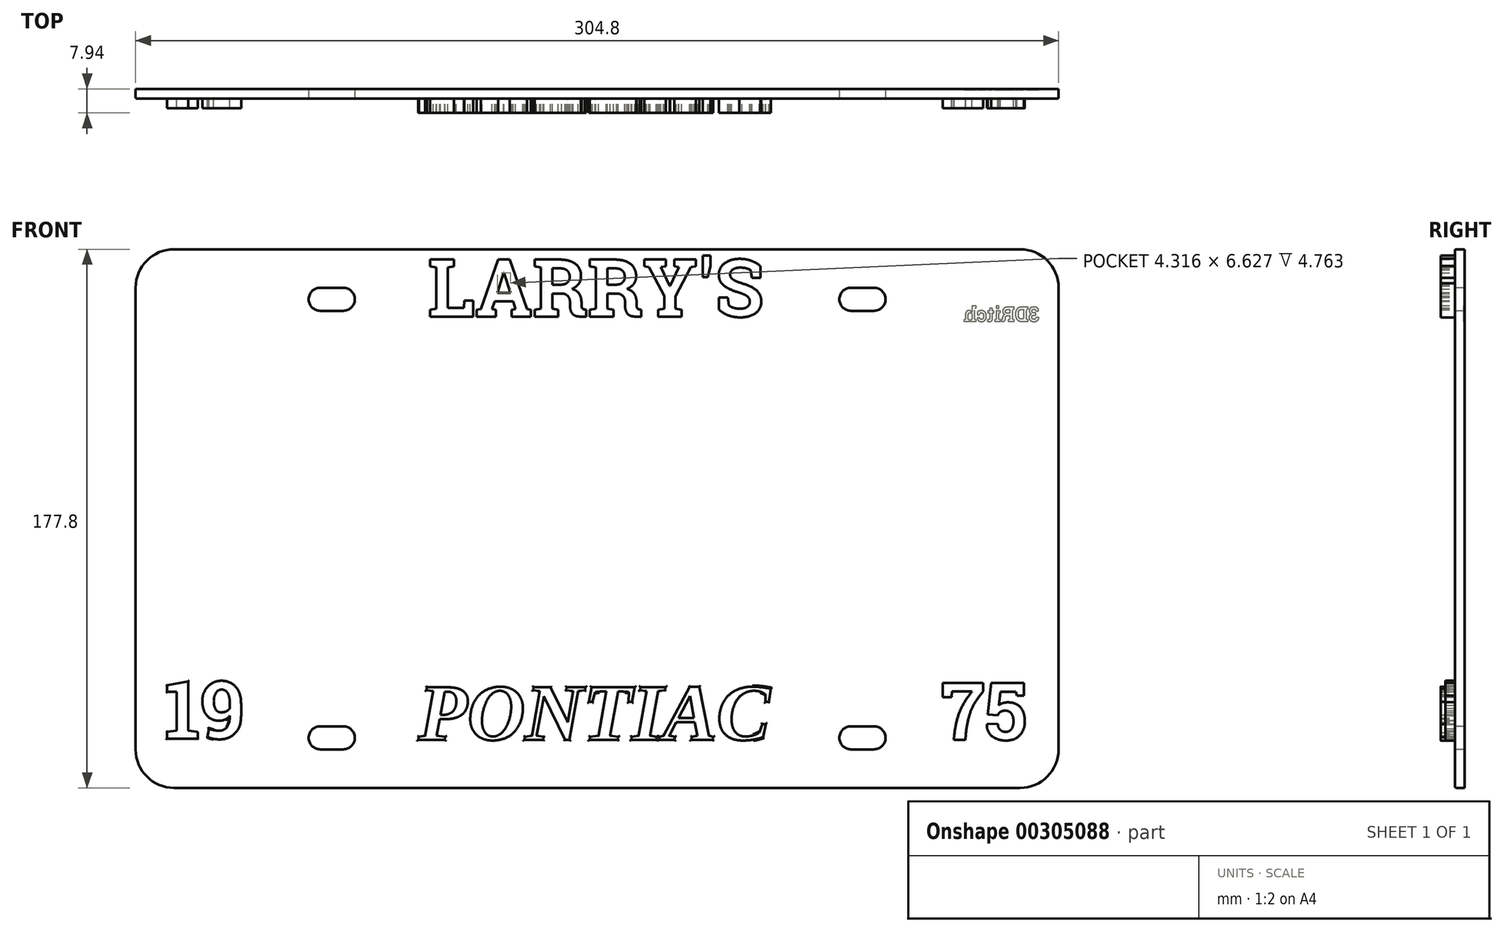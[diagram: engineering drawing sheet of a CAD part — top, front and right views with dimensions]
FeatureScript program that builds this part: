
annotation { "Feature Type Name" : "Feature", "Feature Type Description" : "" }
export const myFeature = defineFeature(function(context is Context, id is Id, definition is map)
    precondition{}
    {
        {
            var Q0;
            Q0=qCreatedBy(makeId("Front.planeOp"),FACE);
            var sketch = newSketch(context, id + "F0", { "sketchPlane" : qUnion([Q0])});
            skLineSegment(sketch, "E0.bottom", {"start": v(139.7, -88.9) * mm, "end": v(-139.7, -88.9) * mm});
            skLineSegment(sketch, "E0.top", {"start": v(139.7, 88.9) * mm, "end": v(-139.7, 88.9) * mm});
            skLineSegment(sketch, "E0.left", {"start": v(152.4, -76.2) * mm, "end": v(152.4, 76.2) * mm});
            skLineSegment(sketch, "E0.right", {"start": v(-152.4, -76.2) * mm, "end": v(-152.4, 76.2) * mm});
            skPoint(sketch, "E0.middle", {"position": v(0, 0) * mm});
            skLineSegment(sketch, "E1.bottom", {"start": v(-91.44, 76.2) * mm, "end": v(-83.82, 76.2) * mm, "construction": true});
            skLineSegment(sketch, "E1.top", {"start": v(-91.44, 68.58) * mm, "end": v(-83.82, 68.58) * mm, "construction": true});
            skPoint(sketch, "E1.middle", {"position": v(-87.63, 72.4) * mm});
            skPoint(sketch, "E2.visualSharp", {"position": v(-152.4, 88.9) * mm});
            skArc(sketch, "E2.filletArc", {"start": v(-139.7, 88.9) * mm, "mid": v(-148.68, 85.18) * mm, "end": v(-152.4, 76.2) * mm});
            skPoint(sketch, "E3.visualSharp", {"position": v(152.4, 88.9) * mm});
            skArc(sketch, "E3.filletArc", {"start": v(152.4, 76.2) * mm, "mid": v(148.68, 85.18) * mm, "end": v(139.7, 88.9) * mm});
            skPoint(sketch, "E4.visualSharp", {"position": v(152.4, -88.9) * mm});
            skArc(sketch, "E4.filletArc", {"start": v(139.7, -88.9) * mm, "mid": v(148.68, -85.18) * mm, "end": v(152.4, -76.2) * mm});
            skPoint(sketch, "E5.visualSharp", {"position": v(-152.4, -88.9) * mm});
            skArc(sketch, "E5.filletArc", {"start": v(-152.4, -76.2) * mm, "mid": v(-148.68, -85.18) * mm, "end": v(-139.7, -88.9) * mm});
            skArc(sketch, "E6", {"start": v(-91.44, 76.2) * mm, "mid": v(-95.25, 72.4) * mm, "end": v(-91.44, 68.58) * mm, "construction": true});
            skArc(sketch, "E7", {"start": v(-83.82, 68.58) * mm, "mid": v(-80.01, 72.39) * mm, "end": v(-83.82, 76.2) * mm, "construction": true});
            skSolve(sketch);
        }
        {
            var Q0;
            Q0=makeQuery(id+"F0.imprint","IMPRINT",FACE,{"disambiguationData":[TD([[makeQuery(id+"F0.imprint","IMPRINT",EDGE,{"derivedFrom":sQuery(id+"F0.wireOp",EDGE,"E0.bottom")}),-1.0]])]});
            extrude(context, id + "F1", {"entities" : qUnion([Q0]), "depth" : 3.17 * mm});
        }
        {
            var Q0;
            Q0=makeQuery(id+"F1.opExtrude","CAP_FACE",FACE,{"disambiguationData":[OSD([sQuery(id+"F0.wireOp",EDGE,"E0.bottom"),sQuery(id+"F0.wireOp",EDGE,"E0.top"),sQuery(id+"F0.wireOp",EDGE,"E0.left"),sQuery(id+"F0.wireOp",EDGE,"E0.right"),sQuery(id+"F0.wireOp",EDGE,"E2.filletArc"),sQuery(id+"F0.wireOp",EDGE,"E3.filletArc"),sQuery(id+"F0.wireOp",EDGE,"E4.filletArc"),sQuery(id+"F0.wireOp",EDGE,"E5.filletArc")])],"isStart":false});
            var sketch = newSketch(context, id + "F2", { "sketchPlane" : qUnion([Q0])});
            skArc(sketch, "E8.0", {"start": v(-91.44, 76.2) * mm, "mid": v(-95.25, 72.4) * mm, "end": v(-91.44, 68.58) * mm});
            skArc(sketch, "E8.1", {"start": v(-83.82, 68.58) * mm, "mid": v(-80.01, 72.39) * mm, "end": v(-83.82, 76.2) * mm});
            skLineSegment(sketch, "E9.0", {"start": v(-91.44, 76.2) * mm, "end": v(-83.82, 76.2) * mm});
            skLineSegment(sketch, "E10.0", {"start": v(-91.44, 68.58) * mm, "end": v(-83.82, 68.58) * mm});
            skLineSegment(sketch, "E11.0.1.0", {"start": v(-91.44, -68.58) * mm, "end": v(-83.82, -68.58) * mm});
            skLineSegment(sketch, "E11.0.1.1", {"start": v(-91.44, -76.2) * mm, "end": v(-83.82, -76.2) * mm});
            skArc(sketch, "E11.0.1.2", {"start": v(-91.44, -68.58) * mm, "mid": v(-95.25, -72.39) * mm, "end": v(-91.44, -76.2) * mm});
            skArc(sketch, "E11.0.1.3", {"start": v(-83.82, -76.2) * mm, "mid": v(-80.01, -72.4) * mm, "end": v(-83.82, -68.58) * mm});
            skLineSegment(sketch, "E11.1.0.0", {"start": v(83.82, 76.2) * mm, "end": v(91.44, 76.2) * mm});
            skLineSegment(sketch, "E11.1.0.1", {"start": v(83.82, 68.58) * mm, "end": v(91.44, 68.58) * mm});
            skArc(sketch, "E11.1.0.2", {"start": v(83.82, 76.2) * mm, "mid": v(80.01, 72.4) * mm, "end": v(83.82, 68.58) * mm});
            skArc(sketch, "E11.1.0.3", {"start": v(91.44, 68.58) * mm, "mid": v(95.25, 72.39) * mm, "end": v(91.44, 76.2) * mm});
            skLineSegment(sketch, "E11.1.1.0", {"start": v(83.82, -68.58) * mm, "end": v(91.44, -68.58) * mm});
            skLineSegment(sketch, "E11.1.1.1", {"start": v(83.82, -76.2) * mm, "end": v(91.44, -76.2) * mm});
            skArc(sketch, "E11.1.1.2", {"start": v(83.82, -68.58) * mm, "mid": v(80.01, -72.39) * mm, "end": v(83.82, -76.2) * mm});
            skArc(sketch, "E11.1.1.3", {"start": v(91.44, -76.2) * mm, "mid": v(95.25, -72.4) * mm, "end": v(91.44, -68.58) * mm});
            skLineSegment(sketch, "E11.direction1", {"start": v(-91.44, 76.2) * mm, "end": v(83.82, 76.2) * mm, "construction": true});
            skLineSegment(sketch, "E11.direction2", {"start": v(-91.44, 76.2) * mm, "end": v(-91.44, -68.58) * mm, "construction": true});
            skSolve(sketch);
        }
        {
            var Q0;
            Q0=makeQuery(id+"F2.imprint","IMPRINT",FACE,{"disambiguationData":[TD([[makeQuery(id+"F2.imprint","IMPRINT",EDGE,{"derivedFrom":sQuery(id+"F2.wireOp",EDGE,"E8.0")}),1.0]])]});
            var Q1;
            Q1=makeQuery(id+"F2.imprint","IMPRINT",FACE,{"disambiguationData":[TD([[makeQuery(id+"F2.imprint","IMPRINT",EDGE,{"derivedFrom":sQuery(id+"F2.wireOp",EDGE,"E11.0.1.0")}),-1.0]])]});
            var Q2;
            Q2=makeQuery(id+"F2.imprint","IMPRINT",FACE,{"disambiguationData":[TD([[makeQuery(id+"F2.imprint","IMPRINT",EDGE,{"derivedFrom":sQuery(id+"F2.wireOp",EDGE,"E11.1.1.0")}),-1.0]])]});
            var Q3;
            Q3=makeQuery(id+"F2.imprint","IMPRINT",FACE,{"disambiguationData":[TD([[makeQuery(id+"F2.imprint","IMPRINT",EDGE,{"derivedFrom":sQuery(id+"F2.wireOp",EDGE,"E11.1.0.0")}),-1.0]])]});
            var Q4;
            Q4=sQuery(id+"F2.wireOp",EDGE,"E9.0");
            extrude(context, id + "F3", {"entities" : qUnion([Q0, Q1, Q2, Q3]), "operationType" : NewBodyOperationType.REMOVE, "surfaceEntities" : qUnion([Q4]), "endBound" : BoundingType.THROUGH_ALL, "oppositeDirection" : true, "depth" : 25.4 * mm});
        }
        {
            var Q0;
            {var subQ0=sQuery(id+"F0.wireOp",EDGE,"E5.filletArc");var subQ1=sQuery(id+"F0.wireOp",EDGE,"E4.filletArc");var subQ2=sQuery(id+"F0.wireOp",EDGE,"E0.left");var subQ3=sQuery(id+"F0.wireOp",EDGE,"E0.top");var subQ4=sQuery(id+"F0.wireOp",EDGE,"E0.right");var subQ5=sQuery(id+"F0.wireOp",EDGE,"E2.filletArc");var subQ6=sQuery(id+"F0.wireOp",EDGE,"E0.bottom");var subQ7=sQuery(id+"F0.wireOp",EDGE,"E3.filletArc");Q0=makeQuery(id+"FR5AeGaN4UOH5Dw_1.boolean.opBoolean","SPLIT",FACE,{"disambiguationData":[TD([makeQuery(id+"F1.opExtrude","SWEPT_FACE",FACE,{"disambiguationData":[OSD([subQ6])]})])],"derivedFrom":makeQuery(id+"F1.opExtrude","CAP_FACE",FACE,{"disambiguationData":[OSD([subQ6,subQ3,subQ2,subQ4,subQ5,subQ7,subQ1,subQ0])],"isStart":false})});}
            var sketch = newSketch(context, id + "F4", { "sketchPlane" : qUnion([Q0])});
            skText(sketch, "E12", { "text": "PONTIAC", "fontName": "Tinos-BoldItalic.ttf"});
            const initialGuessF4  = {"E12": [-0.05902, -0.07303, 1, 0, 0.01905]};
            skSetInitialGuess(sketch, initialGuessF4);
            skSolve(sketch);
        }
        {
            var Q0;
            Q0=qSketchRegion(id+"F4",true);
            extrude(context, id + "F5", {"entities" : qUnion([Q0]), "operationType" : NewBodyOperationType.ADD, "depth" : 4.76 * mm});
        }
        {
            var Q0;
            Q0=makeQuery(id+"FR5AeGaN4UOH5Dw_1.opExtrude","CAP_FACE",FACE,{"disambiguationData":[OSD([sQuery(id+"FcNhi3Mizf4jFf0_1.wireOp",EDGE,"8683c3fa-c94f-43aa-a8e3-5249f5e40e1b.sketch_text.stroke-51"),sQuery(id+"FcNhi3Mizf4jFf0_1.wireOp",EDGE,"8683c3fa-c94f-43aa-a8e3-5249f5e40e1b.sketch_text.stroke-52"),sQuery(id+"FcNhi3Mizf4jFf0_1.wireOp",EDGE,"8683c3fa-c94f-43aa-a8e3-5249f5e40e1b.sketch_text.stroke-53"),sQuery(id+"FcNhi3Mizf4jFf0_1.wireOp",EDGE,"8683c3fa-c94f-43aa-a8e3-5249f5e40e1b.sketch_text.stroke-54"),sQuery(id+"FcNhi3Mizf4jFf0_1.wireOp",EDGE,"8683c3fa-c94f-43aa-a8e3-5249f5e40e1b.sketch_text.stroke-55"),sQuery(id+"FcNhi3Mizf4jFf0_1.wireOp",EDGE,"8683c3fa-c94f-43aa-a8e3-5249f5e40e1b.sketch_text.stroke-56"),sQuery(id+"FcNhi3Mizf4jFf0_1.wireOp",EDGE,"8683c3fa-c94f-43aa-a8e3-5249f5e40e1b.sketch_text.stroke-57"),sQuery(id+"FcNhi3Mizf4jFf0_1.wireOp",EDGE,"8683c3fa-c94f-43aa-a8e3-5249f5e40e1b.sketch_text.stroke-58"),sQuery(id+"FcNhi3Mizf4jFf0_1.wireOp",EDGE,"8683c3fa-c94f-43aa-a8e3-5249f5e40e1b.sketch_text.stroke-59"),sQuery(id+"FcNhi3Mizf4jFf0_1.wireOp",EDGE,"8683c3fa-c94f-43aa-a8e3-5249f5e40e1b.sketch_text.stroke-60"),sQuery(id+"FcNhi3Mizf4jFf0_1.wireOp",EDGE,"8683c3fa-c94f-43aa-a8e3-5249f5e40e1b.sketch_text.stroke-61"),sQuery(id+"FcNhi3Mizf4jFf0_1.wireOp",EDGE,"8683c3fa-c94f-43aa-a8e3-5249f5e40e1b.sketch_text.stroke-62"),sQuery(id+"FcNhi3Mizf4jFf0_1.wireOp",EDGE,"8683c3fa-c94f-43aa-a8e3-5249f5e40e1b.sketch_text.stroke-63"),sQuery(id+"FcNhi3Mizf4jFf0_1.wireOp",EDGE,"8683c3fa-c94f-43aa-a8e3-5249f5e40e1b.sketch_text.stroke-64"),sQuery(id+"FcNhi3Mizf4jFf0_1.wireOp",EDGE,"8683c3fa-c94f-43aa-a8e3-5249f5e40e1b.sketch_text.stroke-65"),sQuery(id+"FcNhi3Mizf4jFf0_1.wireOp",EDGE,"8683c3fa-c94f-43aa-a8e3-5249f5e40e1b.sketch_text.stroke-66"),sQuery(id+"FcNhi3Mizf4jFf0_1.wireOp",EDGE,"8683c3fa-c94f-43aa-a8e3-5249f5e40e1b.sketch_text.stroke-67"),sQuery(id+"FcNhi3Mizf4jFf0_1.wireOp",EDGE,"8683c3fa-c94f-43aa-a8e3-5249f5e40e1b.sketch_text.stroke-68"),sQuery(id+"FcNhi3Mizf4jFf0_1.wireOp",EDGE,"8683c3fa-c94f-43aa-a8e3-5249f5e40e1b.sketch_text.stroke-69")])],"isStart":false});
            var Q1;
            Q1=makeQuery(id+"FR5AeGaN4UOH5Dw_1.opExtrude","CAP_FACE",FACE,{"disambiguationData":[OSD([sQuery(id+"FcNhi3Mizf4jFf0_1.wireOp",EDGE,"8683c3fa-c94f-43aa-a8e3-5249f5e40e1b.sketch_text.stroke-70"),sQuery(id+"FcNhi3Mizf4jFf0_1.wireOp",EDGE,"8683c3fa-c94f-43aa-a8e3-5249f5e40e1b.sketch_text.stroke-71"),sQuery(id+"FcNhi3Mizf4jFf0_1.wireOp",EDGE,"8683c3fa-c94f-43aa-a8e3-5249f5e40e1b.sketch_text.stroke-72"),sQuery(id+"FcNhi3Mizf4jFf0_1.wireOp",EDGE,"8683c3fa-c94f-43aa-a8e3-5249f5e40e1b.sketch_text.stroke-73"),sQuery(id+"FcNhi3Mizf4jFf0_1.wireOp",EDGE,"8683c3fa-c94f-43aa-a8e3-5249f5e40e1b.sketch_text.stroke-74"),sQuery(id+"FcNhi3Mizf4jFf0_1.wireOp",EDGE,"8683c3fa-c94f-43aa-a8e3-5249f5e40e1b.sketch_text.stroke-75"),sQuery(id+"FcNhi3Mizf4jFf0_1.wireOp",EDGE,"8683c3fa-c94f-43aa-a8e3-5249f5e40e1b.sketch_text.stroke-76"),sQuery(id+"FcNhi3Mizf4jFf0_1.wireOp",EDGE,"8683c3fa-c94f-43aa-a8e3-5249f5e40e1b.sketch_text.stroke-77"),sQuery(id+"FcNhi3Mizf4jFf0_1.wireOp",EDGE,"8683c3fa-c94f-43aa-a8e3-5249f5e40e1b.sketch_text.stroke-78"),sQuery(id+"FcNhi3Mizf4jFf0_1.wireOp",EDGE,"8683c3fa-c94f-43aa-a8e3-5249f5e40e1b.sketch_text.stroke-79"),sQuery(id+"FcNhi3Mizf4jFf0_1.wireOp",EDGE,"8683c3fa-c94f-43aa-a8e3-5249f5e40e1b.sketch_text.stroke-80"),sQuery(id+"FcNhi3Mizf4jFf0_1.wireOp",EDGE,"8683c3fa-c94f-43aa-a8e3-5249f5e40e1b.sketch_text.stroke-81"),sQuery(id+"FcNhi3Mizf4jFf0_1.wireOp",EDGE,"8683c3fa-c94f-43aa-a8e3-5249f5e40e1b.sketch_text.stroke-82"),sQuery(id+"FcNhi3Mizf4jFf0_1.wireOp",EDGE,"8683c3fa-c94f-43aa-a8e3-5249f5e40e1b.sketch_text.stroke-83"),sQuery(id+"FcNhi3Mizf4jFf0_1.wireOp",EDGE,"8683c3fa-c94f-43aa-a8e3-5249f5e40e1b.sketch_text.stroke-84"),sQuery(id+"FcNhi3Mizf4jFf0_1.wireOp",EDGE,"8683c3fa-c94f-43aa-a8e3-5249f5e40e1b.sketch_text.stroke-85"),sQuery(id+"FcNhi3Mizf4jFf0_1.wireOp",EDGE,"8683c3fa-c94f-43aa-a8e3-5249f5e40e1b.sketch_text.stroke-86"),sQuery(id+"FcNhi3Mizf4jFf0_1.wireOp",EDGE,"8683c3fa-c94f-43aa-a8e3-5249f5e40e1b.sketch_text.stroke-87"),sQuery(id+"FcNhi3Mizf4jFf0_1.wireOp",EDGE,"8683c3fa-c94f-43aa-a8e3-5249f5e40e1b.sketch_text.stroke-88")])],"isStart":false});
            var Q2;
            Q2=makeQuery(id+"FR5AeGaN4UOH5Dw_1.opExtrude","CAP_FACE",FACE,{"disambiguationData":[OSD([sQuery(id+"FcNhi3Mizf4jFf0_1.wireOp",EDGE,"8683c3fa-c94f-43aa-a8e3-5249f5e40e1b.sketch_text.stroke-89"),sQuery(id+"FcNhi3Mizf4jFf0_1.wireOp",EDGE,"8683c3fa-c94f-43aa-a8e3-5249f5e40e1b.sketch_text.stroke-90"),sQuery(id+"FcNhi3Mizf4jFf0_1.wireOp",EDGE,"8683c3fa-c94f-43aa-a8e3-5249f5e40e1b.sketch_text.stroke-91"),sQuery(id+"FcNhi3Mizf4jFf0_1.wireOp",EDGE,"8683c3fa-c94f-43aa-a8e3-5249f5e40e1b.sketch_text.stroke-92"),sQuery(id+"FcNhi3Mizf4jFf0_1.wireOp",EDGE,"8683c3fa-c94f-43aa-a8e3-5249f5e40e1b.sketch_text.stroke-93"),sQuery(id+"FcNhi3Mizf4jFf0_1.wireOp",EDGE,"8683c3fa-c94f-43aa-a8e3-5249f5e40e1b.sketch_text.stroke-94"),sQuery(id+"FcNhi3Mizf4jFf0_1.wireOp",EDGE,"8683c3fa-c94f-43aa-a8e3-5249f5e40e1b.sketch_text.stroke-95"),sQuery(id+"FcNhi3Mizf4jFf0_1.wireOp",EDGE,"8683c3fa-c94f-43aa-a8e3-5249f5e40e1b.sketch_text.stroke-96"),sQuery(id+"FcNhi3Mizf4jFf0_1.wireOp",EDGE,"8683c3fa-c94f-43aa-a8e3-5249f5e40e1b.sketch_text.stroke-97"),sQuery(id+"FcNhi3Mizf4jFf0_1.wireOp",EDGE,"8683c3fa-c94f-43aa-a8e3-5249f5e40e1b.sketch_text.stroke-98"),sQuery(id+"FcNhi3Mizf4jFf0_1.wireOp",EDGE,"8683c3fa-c94f-43aa-a8e3-5249f5e40e1b.sketch_text.stroke-99"),sQuery(id+"FcNhi3Mizf4jFf0_1.wireOp",EDGE,"8683c3fa-c94f-43aa-a8e3-5249f5e40e1b.sketch_text.stroke-100"),sQuery(id+"FcNhi3Mizf4jFf0_1.wireOp",EDGE,"8683c3fa-c94f-43aa-a8e3-5249f5e40e1b.sketch_text.stroke-101"),sQuery(id+"FcNhi3Mizf4jFf0_1.wireOp",EDGE,"8683c3fa-c94f-43aa-a8e3-5249f5e40e1b.sketch_text.stroke-102"),sQuery(id+"FcNhi3Mizf4jFf0_1.wireOp",EDGE,"8683c3fa-c94f-43aa-a8e3-5249f5e40e1b.sketch_text.stroke-103"),sQuery(id+"FcNhi3Mizf4jFf0_1.wireOp",EDGE,"8683c3fa-c94f-43aa-a8e3-5249f5e40e1b.sketch_text.stroke-104"),sQuery(id+"FcNhi3Mizf4jFf0_1.wireOp",EDGE,"8683c3fa-c94f-43aa-a8e3-5249f5e40e1b.sketch_text.stroke-105"),sQuery(id+"FcNhi3Mizf4jFf0_1.wireOp",EDGE,"8683c3fa-c94f-43aa-a8e3-5249f5e40e1b.sketch_text.stroke-106"),sQuery(id+"FcNhi3Mizf4jFf0_1.wireOp",EDGE,"8683c3fa-c94f-43aa-a8e3-5249f5e40e1b.sketch_text.stroke-107"),sQuery(id+"FcNhi3Mizf4jFf0_1.wireOp",EDGE,"8683c3fa-c94f-43aa-a8e3-5249f5e40e1b.sketch_text.stroke-108"),sQuery(id+"FcNhi3Mizf4jFf0_1.wireOp",EDGE,"8683c3fa-c94f-43aa-a8e3-5249f5e40e1b.sketch_text.stroke-109"),sQuery(id+"FcNhi3Mizf4jFf0_1.wireOp",EDGE,"8683c3fa-c94f-43aa-a8e3-5249f5e40e1b.sketch_text.stroke-110"),sQuery(id+"FcNhi3Mizf4jFf0_1.wireOp",EDGE,"8683c3fa-c94f-43aa-a8e3-5249f5e40e1b.sketch_text.stroke-111"),sQuery(id+"FcNhi3Mizf4jFf0_1.wireOp",EDGE,"8683c3fa-c94f-43aa-a8e3-5249f5e40e1b.sketch_text.stroke-112"),sQuery(id+"FcNhi3Mizf4jFf0_1.wireOp",EDGE,"8683c3fa-c94f-43aa-a8e3-5249f5e40e1b.sketch_text.stroke-113"),sQuery(id+"FcNhi3Mizf4jFf0_1.wireOp",EDGE,"8683c3fa-c94f-43aa-a8e3-5249f5e40e1b.sketch_text.stroke-114")])],"isStart":false});
            var Q3;
            Q3=makeQuery(id+"FR5AeGaN4UOH5Dw_1.opExtrude","CAP_FACE",FACE,{"disambiguationData":[OSD([sQuery(id+"FcNhi3Mizf4jFf0_1.wireOp",EDGE,"8683c3fa-c94f-43aa-a8e3-5249f5e40e1b.sketch_text.stroke-115"),sQuery(id+"FcNhi3Mizf4jFf0_1.wireOp",EDGE,"8683c3fa-c94f-43aa-a8e3-5249f5e40e1b.sketch_text.stroke-116"),sQuery(id+"FcNhi3Mizf4jFf0_1.wireOp",EDGE,"8683c3fa-c94f-43aa-a8e3-5249f5e40e1b.sketch_text.stroke-117"),sQuery(id+"FcNhi3Mizf4jFf0_1.wireOp",EDGE,"8683c3fa-c94f-43aa-a8e3-5249f5e40e1b.sketch_text.stroke-118"),sQuery(id+"FcNhi3Mizf4jFf0_1.wireOp",EDGE,"8683c3fa-c94f-43aa-a8e3-5249f5e40e1b.sketch_text.stroke-119")])],"isStart":false});
            var Q4;
            Q4=makeQuery(id+"FR5AeGaN4UOH5Dw_1.opExtrude","CAP_FACE",FACE,{"disambiguationData":[OSD([sQuery(id+"FcNhi3Mizf4jFf0_1.wireOp",EDGE,"8683c3fa-c94f-43aa-a8e3-5249f5e40e1b.sketch_text.stroke-120"),sQuery(id+"FcNhi3Mizf4jFf0_1.wireOp",EDGE,"8683c3fa-c94f-43aa-a8e3-5249f5e40e1b.sketch_text.stroke-121"),sQuery(id+"FcNhi3Mizf4jFf0_1.wireOp",EDGE,"8683c3fa-c94f-43aa-a8e3-5249f5e40e1b.sketch_text.stroke-122"),sQuery(id+"FcNhi3Mizf4jFf0_1.wireOp",EDGE,"8683c3fa-c94f-43aa-a8e3-5249f5e40e1b.sketch_text.stroke-123"),sQuery(id+"FcNhi3Mizf4jFf0_1.wireOp",EDGE,"8683c3fa-c94f-43aa-a8e3-5249f5e40e1b.sketch_text.stroke-124"),sQuery(id+"FcNhi3Mizf4jFf0_1.wireOp",EDGE,"8683c3fa-c94f-43aa-a8e3-5249f5e40e1b.sketch_text.stroke-125"),sQuery(id+"FcNhi3Mizf4jFf0_1.wireOp",EDGE,"8683c3fa-c94f-43aa-a8e3-5249f5e40e1b.sketch_text.stroke-126"),sQuery(id+"FcNhi3Mizf4jFf0_1.wireOp",EDGE,"8683c3fa-c94f-43aa-a8e3-5249f5e40e1b.sketch_text.stroke-127"),sQuery(id+"FcNhi3Mizf4jFf0_1.wireOp",EDGE,"8683c3fa-c94f-43aa-a8e3-5249f5e40e1b.sketch_text.stroke-128"),sQuery(id+"FcNhi3Mizf4jFf0_1.wireOp",EDGE,"8683c3fa-c94f-43aa-a8e3-5249f5e40e1b.sketch_text.stroke-129"),sQuery(id+"FcNhi3Mizf4jFf0_1.wireOp",EDGE,"8683c3fa-c94f-43aa-a8e3-5249f5e40e1b.sketch_text.stroke-130"),sQuery(id+"FcNhi3Mizf4jFf0_1.wireOp",EDGE,"8683c3fa-c94f-43aa-a8e3-5249f5e40e1b.sketch_text.stroke-131"),sQuery(id+"FcNhi3Mizf4jFf0_1.wireOp",EDGE,"8683c3fa-c94f-43aa-a8e3-5249f5e40e1b.sketch_text.stroke-132"),sQuery(id+"FcNhi3Mizf4jFf0_1.wireOp",EDGE,"8683c3fa-c94f-43aa-a8e3-5249f5e40e1b.sketch_text.stroke-133"),sQuery(id+"FcNhi3Mizf4jFf0_1.wireOp",EDGE,"8683c3fa-c94f-43aa-a8e3-5249f5e40e1b.sketch_text.stroke-134"),sQuery(id+"FcNhi3Mizf4jFf0_1.wireOp",EDGE,"8683c3fa-c94f-43aa-a8e3-5249f5e40e1b.sketch_text.stroke-135"),sQuery(id+"FcNhi3Mizf4jFf0_1.wireOp",EDGE,"8683c3fa-c94f-43aa-a8e3-5249f5e40e1b.sketch_text.stroke-136"),sQuery(id+"FcNhi3Mizf4jFf0_1.wireOp",EDGE,"8683c3fa-c94f-43aa-a8e3-5249f5e40e1b.sketch_text.stroke-137"),sQuery(id+"FcNhi3Mizf4jFf0_1.wireOp",EDGE,"8683c3fa-c94f-43aa-a8e3-5249f5e40e1b.sketch_text.stroke-138"),sQuery(id+"FcNhi3Mizf4jFf0_1.wireOp",EDGE,"8683c3fa-c94f-43aa-a8e3-5249f5e40e1b.sketch_text.stroke-139"),sQuery(id+"FcNhi3Mizf4jFf0_1.wireOp",EDGE,"8683c3fa-c94f-43aa-a8e3-5249f5e40e1b.sketch_text.stroke-140"),sQuery(id+"FcNhi3Mizf4jFf0_1.wireOp",EDGE,"8683c3fa-c94f-43aa-a8e3-5249f5e40e1b.sketch_text.stroke-141"),sQuery(id+"FcNhi3Mizf4jFf0_1.wireOp",EDGE,"8683c3fa-c94f-43aa-a8e3-5249f5e40e1b.sketch_text.stroke-142"),sQuery(id+"FcNhi3Mizf4jFf0_1.wireOp",EDGE,"8683c3fa-c94f-43aa-a8e3-5249f5e40e1b.sketch_text.stroke-143"),sQuery(id+"FcNhi3Mizf4jFf0_1.wireOp",EDGE,"8683c3fa-c94f-43aa-a8e3-5249f5e40e1b.sketch_text.stroke-144"),sQuery(id+"FcNhi3Mizf4jFf0_1.wireOp",EDGE,"8683c3fa-c94f-43aa-a8e3-5249f5e40e1b.sketch_text.stroke-145"),sQuery(id+"FcNhi3Mizf4jFf0_1.wireOp",EDGE,"8683c3fa-c94f-43aa-a8e3-5249f5e40e1b.sketch_text.stroke-146"),sQuery(id+"FcNhi3Mizf4jFf0_1.wireOp",EDGE,"8683c3fa-c94f-43aa-a8e3-5249f5e40e1b.sketch_text.stroke-147"),sQuery(id+"FcNhi3Mizf4jFf0_1.wireOp",EDGE,"8683c3fa-c94f-43aa-a8e3-5249f5e40e1b.sketch_text.stroke-148"),sQuery(id+"FcNhi3Mizf4jFf0_1.wireOp",EDGE,"8683c3fa-c94f-43aa-a8e3-5249f5e40e1b.sketch_text.stroke-149")])],"isStart":false});
            var Q5;
            {var subQ72=sQuery(id+"F0.wireOp",EDGE,"E3.filletArc");var subQ83=sQuery(id+"F0.wireOp",EDGE,"E0.bottom");var subQ84=makeQuery(id+"F1.opExtrude","SWEPT_FACE",FACE,{"disambiguationData":[OSD([subQ83])]});var subQ90=sQuery(id+"F0.wireOp",EDGE,"E2.filletArc");var subQ101=sQuery(id+"F0.wireOp",EDGE,"E0.right");var subQ111=sQuery(id+"F0.wireOp",EDGE,"E0.top");var subQ123=sQuery(id+"F0.wireOp",EDGE,"E0.left");var subQ132=sQuery(id+"F0.wireOp",EDGE,"E4.filletArc");var subQ143=sQuery(id+"F0.wireOp",EDGE,"E5.filletArc");Q5=makeQuery(id+"F3kJRBSue7Nx1vK_1.boolean.opBoolean","SPLIT",FACE,{"disambiguationData":[TD([subQ84])],"derivedFrom":makeQuery(id+"F5.boolean.opBoolean","SPLIT",FACE,{"disambiguationData":[TD([subQ84])],"derivedFrom":makeQuery(id+"FR5AeGaN4UOH5Dw_1.boolean.opBoolean","SPLIT",FACE,{"disambiguationData":[TD([subQ84])],"derivedFrom":makeQuery(id+"F1.opExtrude","CAP_FACE",FACE,{"disambiguationData":[OSD([subQ83,subQ111,subQ123,subQ101,subQ90,subQ72,subQ132,subQ143])],"isStart":false})})})});}
            fillet(context, id + "F6", {"entities" : qUnion([Q0, Q1, Q2, Q3, Q4, Q5]), "radius" : 0.38 * mm, "tangentPropagation" : true, "allowEdgeOverflow" : false});
        }
        {
            var Q0;
            {var subQ48=sQuery(id+"F0.wireOp",EDGE,"E5.filletArc");var subQ55=sQuery(id+"F0.wireOp",EDGE,"E4.filletArc");var subQ60=sQuery(id+"F0.wireOp",EDGE,"E0.left");var subQ67=sQuery(id+"F0.wireOp",EDGE,"E0.top");var subQ72=sQuery(id+"F0.wireOp",EDGE,"E0.right");var subQ79=sQuery(id+"F0.wireOp",EDGE,"E2.filletArc");var subQ86=sQuery(id+"F0.wireOp",EDGE,"E0.bottom");var subQ87=makeQuery(id+"F1.opExtrude","SWEPT_FACE",FACE,{"disambiguationData":[OSD([subQ86])]});var subQ93=sQuery(id+"F0.wireOp",EDGE,"E3.filletArc");Q0=makeQuery(id+"F3kJRBSue7Nx1vK_1.boolean.opBoolean","SPLIT",FACE,{"disambiguationData":[TD([subQ87])],"derivedFrom":makeQuery(id+"F5.boolean.opBoolean","SPLIT",FACE,{"disambiguationData":[TD([subQ87])],"derivedFrom":makeQuery(id+"F1.opExtrude","CAP_FACE",FACE,{"disambiguationData":[OSD([subQ86,subQ67,subQ60,subQ72,subQ79,subQ93,subQ55,subQ48])],"isStart":false})})});}
            var sketch = newSketch(context, id + "F7", { "sketchPlane" : qUnion([Q0])});
            skText(sketch, "E13", { "text": "LARRY\'S", "fontName": "RobotoSlab-Bold.ttf"});
            const initialGuessF7  = {"E13": [-0.05583, 0.06668, 1, 0, 0.01905]};
            skSetInitialGuess(sketch, initialGuessF7);
            skSolve(sketch);
        }
        {
            var Q0;
            Q0 = qSketchRegion(id + "F7", true);
            extrude(context, id + "F8", {"entities" : qUnion([Q0]), "operationType" : NewBodyOperationType.ADD, "depth" : 4.76 * mm});
        }
        {
            var Q0;
            {var subQ128=sQuery(id+"F0.wireOp",EDGE,"E5.filletArc");var subQ129=sQuery(id+"F0.wireOp",EDGE,"E4.filletArc");var subQ130=sQuery(id+"F0.wireOp",EDGE,"E3.filletArc");var subQ131=sQuery(id+"F0.wireOp",EDGE,"E2.filletArc");var subQ132=sQuery(id+"F0.wireOp",EDGE,"E0.bottom");var subQ133=sQuery(id+"F0.wireOp",EDGE,"E0.top");var subQ134=sQuery(id+"F0.wireOp",EDGE,"E0.left");var subQ135=sQuery(id+"F0.wireOp",EDGE,"E0.right");var subQ273=makeQuery(id+"F1.opExtrude","SWEPT_FACE",FACE,{"disambiguationData":[OSD([subQ132])]});Q0=makeQuery(id+"F8.boolean.opBoolean","SPLIT",FACE,{"disambiguationData":[TD([makeQuery(id+"F6.opFillet","BLEND_FACE",FACE,{"disambiguationData":[OSD([subQ132])]})])],"derivedFrom":makeQuery(id+"F3kJRBSue7Nx1vK_1.boolean.opBoolean","SPLIT",FACE,{"disambiguationData":[TD([subQ273])],"derivedFrom":makeQuery(id+"F5.boolean.opBoolean","SPLIT",FACE,{"disambiguationData":[TD([subQ273])],"derivedFrom":makeQuery(id+"F1.opExtrude","CAP_FACE",FACE,{"disambiguationData":[OSD([subQ132,subQ133,subQ134,subQ135,subQ131,subQ130,subQ129,subQ128])],"isStart":false})})})});}
            var sketch = newSketch(context, id + "F9", { "sketchPlane" : qUnion([Q0])});
            skText(sketch, "E14", { "text": "19", "fontName": "RobotoSlab-Bold.ttf"});
            const initialGuessF9  = {"E14": [-0.14287, -0.07264, 1, 0, 0.01905]};
            skSetInitialGuess(sketch, initialGuessF9);
            skSolve(sketch);
        }
        {
            var Q0;
            Q0 = qSketchRegion(id + "F9", true);
            extrude(context, id + "F10", {"entities" : qUnion([Q0]), "operationType" : NewBodyOperationType.ADD, "depth" : 3.17 * mm});
        }
        {
            var Q0;
            {var subQ342=sQuery(id+"F0.wireOp",EDGE,"E5.filletArc");var subQ344=sQuery(id+"F0.wireOp",EDGE,"E4.filletArc");var subQ346=sQuery(id+"F0.wireOp",EDGE,"E3.filletArc");var subQ348=sQuery(id+"F0.wireOp",EDGE,"E2.filletArc");var subQ350=sQuery(id+"F0.wireOp",EDGE,"E0.bottom");var subQ351=makeQuery(id+"F6.opFillet","BLEND_FACE",FACE,{"disambiguationData":[OSD([subQ350])]});var subQ352=sQuery(id+"F0.wireOp",EDGE,"E0.top");var subQ354=sQuery(id+"F0.wireOp",EDGE,"E0.left");var subQ356=sQuery(id+"F0.wireOp",EDGE,"E0.right");var subQ606=makeQuery(id+"F1.opExtrude","SWEPT_FACE",FACE,{"disambiguationData":[OSD([subQ350])]});Q0=makeQuery(id+"F10.boolean.opBoolean","SPLIT",FACE,{"disambiguationData":[TD([subQ351])],"derivedFrom":makeQuery(id+"F8.boolean.opBoolean","SPLIT",FACE,{"disambiguationData":[TD([subQ351])],"derivedFrom":makeQuery(id+"F3kJRBSue7Nx1vK_1.boolean.opBoolean","SPLIT",FACE,{"disambiguationData":[TD([subQ606])],"derivedFrom":makeQuery(id+"F5.boolean.opBoolean","SPLIT",FACE,{"disambiguationData":[TD([subQ606])],"derivedFrom":makeQuery(id+"F1.opExtrude","CAP_FACE",FACE,{"disambiguationData":[OSD([subQ350,subQ352,subQ354,subQ356,subQ348,subQ346,subQ344,subQ342])],"isStart":false})})})})});}
            var sketch = newSketch(context, id + "F11", { "sketchPlane" : qUnion([Q0])});
            skText(sketch, "E15", { "text": "75", "fontName": "RobotoSlab-Bold.ttf"});
            const initialGuessF11  = {"E15": [0.11353, -0.07303, 1, 0, 0.01905]};
            skSetInitialGuess(sketch, initialGuessF11);
            skSolve(sketch);
        }
        {
            var Q0;
            Q0 = qSketchRegion(id + "F11", true);
            extrude(context, id + "F12", {"entities" : qUnion([Q0]), "operationType" : NewBodyOperationType.ADD, "depth" : 3.17 * mm});
        }
        {
            var Q0;
            Q0=makeQuery(id+"F10.opExtrude","CAP_EDGE",EDGE,{"disambiguationData":[OSD([sQuery(id+"F9.wireOp",EDGE,"E14.sketch_text.stroke-23")])],"isStart":true});
            var Q1;
            Q1=makeQuery(id+"F10.opExtrude","CAP_EDGE",EDGE,{"disambiguationData":[OSD([sQuery(id+"F9.wireOp",EDGE,"E14.sketch_text.stroke-33")])],"isStart":true});
            var Q2;
            Q2=makeQuery(id+"F10.opExtrude","CAP_EDGE",EDGE,{"disambiguationData":[OSD([sQuery(id+"F9.wireOp",EDGE,"E14.sketch_text.stroke-8")])],"isStart":true});
            var Q3;
            Q3=makeQuery(id+"F10.opExtrude","CAP_EDGE",EDGE,{"disambiguationData":[OSD([sQuery(id+"F9.wireOp",EDGE,"E14.sketch_text.stroke-5")])],"isStart":true});
            var Q4;
            Q4=makeQuery(id+"F10.opExtrude","CAP_EDGE",EDGE,{"disambiguationData":[OSD([sQuery(id+"F9.wireOp",EDGE,"E14.sketch_text.stroke-7")])],"isStart":true});
            var Q5;
            Q5=makeQuery(id+"F10.opExtrude","CAP_EDGE",EDGE,{"disambiguationData":[OSD([sQuery(id+"F9.wireOp",EDGE,"E14.sketch_text.stroke-9")])],"isStart":true});
            var Q6;
            Q6=makeQuery(id+"F10.opExtrude","CAP_EDGE",EDGE,{"disambiguationData":[OSD([sQuery(id+"F9.wireOp",EDGE,"E14.sketch_text.stroke-1")])],"isStart":true});
            var Q7;
            Q7=makeQuery(id+"F10.opExtrude","CAP_EDGE",EDGE,{"disambiguationData":[OSD([sQuery(id+"F9.wireOp",EDGE,"E14.sketch_text.stroke-2")])],"isStart":true});
            var Q8;
            Q8=makeQuery(id+"F10.opExtrude","CAP_EDGE",EDGE,{"disambiguationData":[OSD([sQuery(id+"F9.wireOp",EDGE,"E14.sketch_text.stroke-3")])],"isStart":true});
            var Q9;
            Q9=makeQuery(id+"F10.opExtrude","CAP_EDGE",EDGE,{"disambiguationData":[OSD([sQuery(id+"F9.wireOp",EDGE,"E14.sketch_text.stroke-4")])],"isStart":true});
            var Q10;
            Q10=makeQuery(id+"F10.opExtrude","CAP_EDGE",EDGE,{"disambiguationData":[OSD([sQuery(id+"F9.wireOp",EDGE,"E14.sketch_text.stroke-0")])],"isStart":true});
            var Q11;
            Q11=makeQuery(id+"F10.opExtrude","SWEPT_FACE",FACE,{"disambiguationData":[OSD([sQuery(id+"F9.wireOp",EDGE,"E14.sketch_text.stroke-6")])]});
            var Q12;
            Q12=makeQuery(id+"F10.opExtrude","CAP_EDGE",EDGE,{"disambiguationData":[OSD([sQuery(id+"F9.wireOp",EDGE,"E14.sketch_text.stroke-10")])],"isStart":true});
            var Q13;
            Q13=makeQuery(id+"F10.opExtrude","CAP_EDGE",EDGE,{"disambiguationData":[OSD([sQuery(id+"F9.wireOp",EDGE,"E14.sketch_text.stroke-28")])],"isStart":true});
            var Q14;
            Q14=makeQuery(id+"F10.opExtrude","CAP_EDGE",EDGE,{"disambiguationData":[OSD([sQuery(id+"F9.wireOp",EDGE,"E14.sketch_text.stroke-27")])],"isStart":true});
            var Q15;
            Q15=makeQuery(id+"F10.opExtrude","CAP_EDGE",EDGE,{"disambiguationData":[OSD([sQuery(id+"F9.wireOp",EDGE,"E14.sketch_text.stroke-26")])],"isStart":true});
            var Q16;
            Q16=makeQuery(id+"F10.opExtrude","CAP_EDGE",EDGE,{"disambiguationData":[OSD([sQuery(id+"F9.wireOp",EDGE,"E14.sketch_text.stroke-15")])],"isStart":true});
            var Q17;
            Q17=makeQuery(id+"F10.opExtrude","CAP_EDGE",EDGE,{"disambiguationData":[OSD([sQuery(id+"F9.wireOp",EDGE,"E14.sketch_text.stroke-12")])],"isStart":true});
            var Q18;
            Q18=makeQuery(id+"F10.opExtrude","SWEPT_EDGE",EDGE,{"disambiguationData":[OSD([sQuery(id+"F9.wireOp",EDGE,"E14.sketch_text.stroke-11"),sQuery(id+"F9.wireOp",EDGE,"E14.sketch_text.stroke-12")])]});
            fillet(context, id + "F13", {"entities" : qUnion([Q0, Q1, Q2, Q3, Q4, Q5, Q6, Q7, Q8, Q9, Q10, Q11, Q12, Q13, Q14, Q15, Q16, Q17, Q18]), "radius" : 0.25 * mm, "tangentPropagation" : true, "allowEdgeOverflow" : false});
        }
        {
            var Q0;
            Q0=makeQuery(id+"F1.opExtrude","CAP_FACE",FACE,{"disambiguationData":[OSD([sQuery(id+"F0.wireOp",EDGE,"E0.bottom"),sQuery(id+"F0.wireOp",EDGE,"E0.top"),sQuery(id+"F0.wireOp",EDGE,"E0.left"),sQuery(id+"F0.wireOp",EDGE,"E0.right"),sQuery(id+"F0.wireOp",EDGE,"E2.filletArc"),sQuery(id+"F0.wireOp",EDGE,"E3.filletArc"),sQuery(id+"F0.wireOp",EDGE,"E4.filletArc"),sQuery(id+"F0.wireOp",EDGE,"E5.filletArc")])],"isStart":true});
            var sketch = newSketch(context, id + "F14", { "sketchPlane" : qUnion([Q0])});
            skText(sketch, "E16", { "text": "3DRitch", "fontName": "RobotoSlab-Bold.ttf"});
            const initialGuessF14  = {"E16": [-0.14605, 0.06509, 1, 0, 0.00476]};
            skSetInitialGuess(sketch, initialGuessF14);
            skSolve(sketch);
        }
        {
            var Q0;
            Q0 = qSketchRegion(id + "F14", true);
            extrude(context, id + "F15", {"entities" : qUnion([Q0]), "operationType" : NewBodyOperationType.REMOVE, "oppositeDirection" : true, "depth" : 0.25 * mm});
        }
    });
